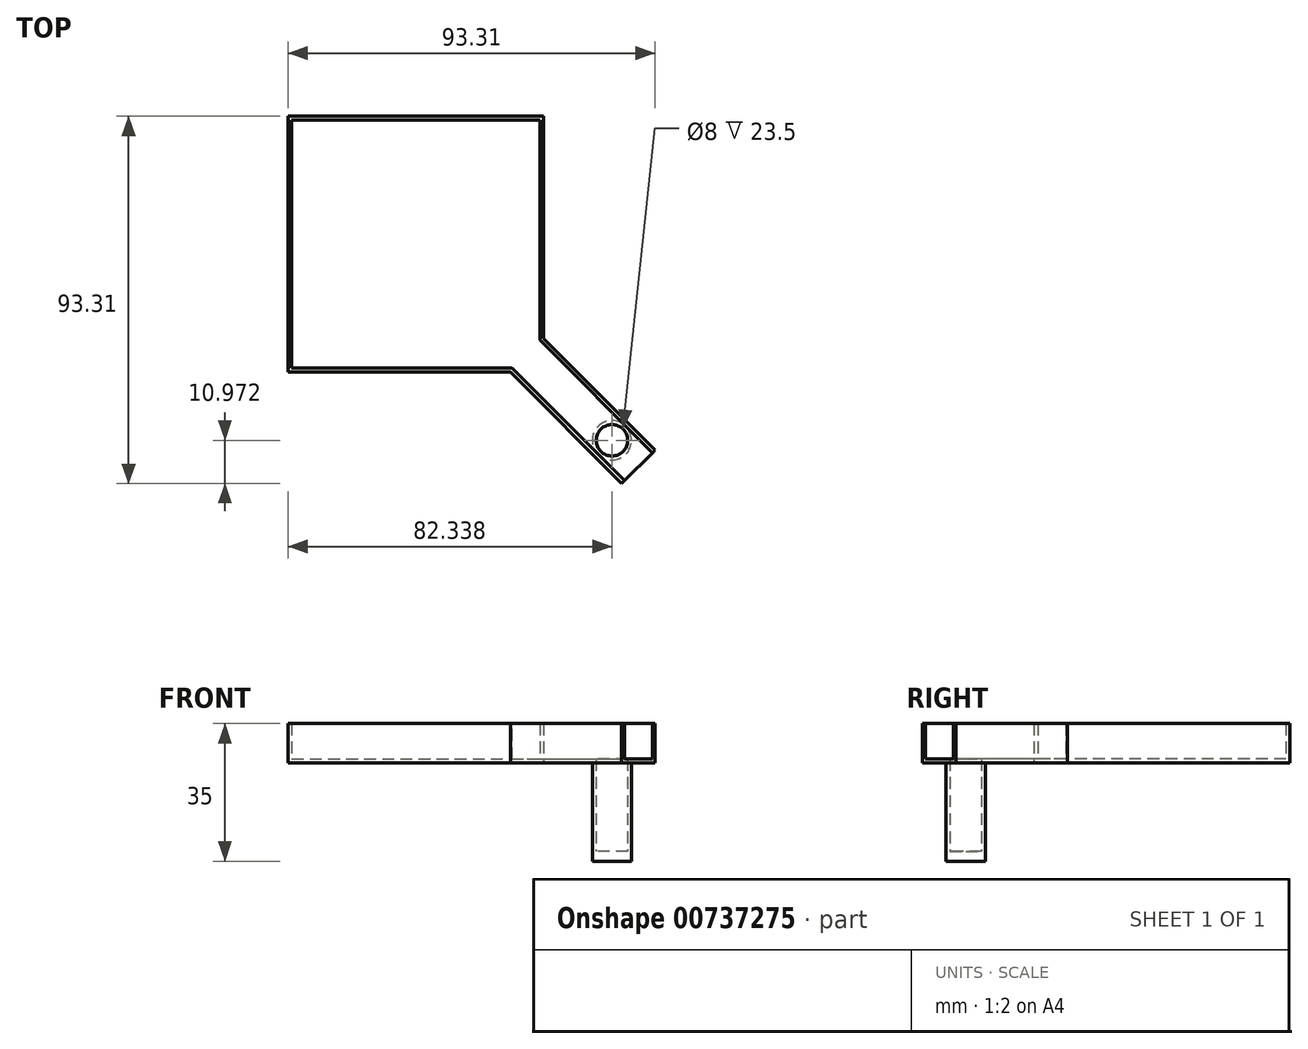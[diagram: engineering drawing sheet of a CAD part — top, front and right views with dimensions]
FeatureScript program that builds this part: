
annotation { "Feature Type Name" : "Feature", "Feature Type Description" : "" }
export const myFeature = defineFeature(function(context is Context, id is Id, definition is map)
    precondition{}
    {
        {
            var Q0;
            Q0=qCreatedBy(makeId("Top.planeOp"),FACE);
            var sketch = newSketch(context, id + "F0", { "sketchPlane" : qUnion([Q0])});
            skLineSegment(sketch, "E0", {"start": v(0, 44.12) * mm, "end": v(0, -39.93) * mm, "construction": true});
            skLineSegment(sketch, "E1", {"start": v(-43.3, 0) * mm, "end": v(40.23, 0) * mm, "construction": true});
            skLineSegment(sketch, "E2.bottom", {"start": v(-32.5, 32.5) * mm, "end": v(32.5, 32.5) * mm});
            skLineSegment(sketch, "E2.top", {"start": v(-32.5, -32.5) * mm, "end": v(32.5, -32.5) * mm});
            skLineSegment(sketch, "E2.left", {"start": v(-32.5, 32.5) * mm, "end": v(-32.5, -32.5) * mm});
            skLineSegment(sketch, "E2.right", {"start": v(32.5, 32.5) * mm, "end": v(32.5, -32.5) * mm});
            skSolve(sketch);
        }
        {
            var Q0;
            Q0 = qSketchRegion(id + "F0", true);
            extrude(context, id + "F1", {"entities" : qUnion([Q0]), "depth" : 10 * mm, "offsetDistance" : 25 * mm});
        }
        {
            var Q0;
            Q0=makeQuery(id+"F1.opExtrude","CAP_FACE",FACE,{"disambiguationData":[OSD([sQuery(id+"F0.wireOp",EDGE,"E2.bottom"),sQuery(id+"F0.wireOp",EDGE,"E2.top"),sQuery(id+"F0.wireOp",EDGE,"E2.left"),sQuery(id+"F0.wireOp",EDGE,"E2.right")])],"isStart":false});
            shell(context, id + "F2", {"entities" : qUnion([Q0]), "thickness" : 1 * mm});
        }
        {
            var Q0;
            Q0=qCreatedBy(makeId("Right.planeOp"),FACE);
            var Q1;
            Q1=qCreatedBy(makeId("Front.planeOp"),FACE);
            cPlane(context, id + "F3", {"entities" : qUnion([Q0, Q1]), "cplaneType" : CPlaneType.MID_PLANE, "offset" : 25 * mm, "flipAlignment" : true, "width" : 150 * mm, "height" : 150 * mm});
        }
        {
            var Q0;
            Q0=qCreatedBy(id+"F3.planeOp",FACE);
            cPlane(context, id + "F4", {"entities" : qUnion([Q0]), "cplaneType" : CPlaneType.OFFSET, "offset" : 50 * mm, "width" : 150 * mm, "height" : 150 * mm});
        }
        {
            var Q0;
            Q0=qCreatedBy(id+"F4.planeOp",FACE);
            var sketch = newSketch(context, id + "F5", { "sketchPlane" : qUnion([Q0])});
            skPoint(sketch, "E3.0", {"position": v(0, 5) * mm});
            skLineSegment(sketch, "E4.left", {"start": v(5, 10) * mm, "end": v(5, 1) * mm});
            skLineSegment(sketch, "E4.right", {"start": v(-5, 10) * mm, "end": v(-5, 1) * mm});
            skLineSegment(sketch, "E5.1", {"start": v(6, 0) * mm, "end": v(-6, 0) * mm});
            skLineSegment(sketch, "E5.2", {"start": v(-6, 10) * mm, "end": v(-6, 0) * mm});
            skLineSegment(sketch, "E6.0", {"start": v(5, 1) * mm, "end": v(-5, 1) * mm});
            skLineSegment(sketch, "E7", {"start": v(6, 0) * mm, "end": v(6, 10) * mm});
            skLineSegment(sketch, "E8", {"start": v(6, 10) * mm, "end": v(5, 10) * mm});
            skLineSegment(sketch, "E9", {"start": v(-5, 10) * mm, "end": v(-6, 10) * mm});
            skSolve(sketch);
        }
        {
            var Q0;
            Q0=makeQuery(id+"F5.imprint","IMPRINT",FACE,{"disambiguationData":[TD([[makeQuery(id+"F5.imprint","IMPRINT",EDGE,{"derivedFrom":sQuery(id+"F5.wireOp",EDGE,"E4.left")}),1.0]])]});
            var Q1;
            Q1=makeQuery(id+"F1.opExtrude","SWEPT_BODY",BODY,{"disambiguationData":[OSD([sQuery(id+"F0.wireOp",EDGE,"E2.bottom"),sQuery(id+"F0.wireOp",EDGE,"E2.top"),sQuery(id+"F0.wireOp",EDGE,"E2.left"),sQuery(id+"F0.wireOp",EDGE,"E2.right")])]});
            extrude(context, id + "F6", {"entities" : qUnion([Q0]), "operationType" : NewBodyOperationType.ADD, "endBound" : BoundingType.UP_TO_NEXT, "oppositeDirection" : true, "depth" : 25 * mm, "endBoundEntityBody" : qUnion([Q1]), "offsetDistance" : 25 * mm, "hasSecondDirection" : true, "secondDirectionOppositeDirection" : false, "secondDirectionDepth" : 30 * mm});
        }
        {
            var Q0;
            Q0=qCreatedBy(id+"F4.planeOp",FACE);
            var sketch = newSketch(context, id + "F7", { "sketchPlane" : qUnion([Q0])});
            skLineSegment(sketch, "E10.0", {"start": v(-5, 10) * mm, "end": v(-5, 1) * mm});
            skLineSegment(sketch, "E11.0", {"start": v(5, 1) * mm, "end": v(-5, 1) * mm});
            skLineSegment(sketch, "E12.0", {"start": v(5, 10) * mm, "end": v(5, 1) * mm});
            skLineSegment(sketch, "E13.0", {"start": v(5, 10) * mm, "end": v(0, 10) * mm});
            skLineSegment(sketch, "E14.0", {"start": v(-5, 10) * mm, "end": v(0, 10) * mm});
            skSolve(sketch);
        }
        {
            var Q0;
            Q0=makeQuery(id+"F7.imprint","IMPRINT",FACE,{"disambiguationData":[TD([[makeQuery(id+"F7.imprint","IMPRINT",EDGE,{"derivedFrom":sQuery(id+"F7.wireOp",EDGE,"E10.0")}),1.0]])]});
            extrude(context, id + "F8", {"entities" : qUnion([Q0]), "operationType" : NewBodyOperationType.REMOVE, "oppositeDirection" : true, "depth" : 64.9 * mm, "offsetDistance" : 25 * mm, "hasSecondDirection" : true, "secondDirectionBound" : SecondDirectionBoundingType.THROUGH_ALL, "secondDirectionOppositeDirection" : false, "secondDirectionDepth" : 25 * mm});
        }
        {
            var Q0;
            Q0=qCreatedBy(makeId("Top.planeOp"),FACE);
            var sketch = newSketch(context, id + "F9", { "sketchPlane" : qUnion([Q0])});
            skPoint(sketch, "E15.0", {"position": v(0, 0) * mm});
            skLineSegment(sketch, "E16", {"start": v(0, 0) * mm, "end": v(70.71, -70.71) * mm, "construction": true});
            skLineSegment(sketch, "E17", {"start": v(53.37, -46.3) * mm, "end": v(46.3, -53.37) * mm, "construction": true});
            skCircle(sketch, "E18", {"center": v(49.84, -49.84) * mm, "radius": 5 * mm});
            skSolve(sketch);
        }
        {
            var Q0;
            Q0=makeQuery(id+"F9.imprint","IMPRINT",FACE,{"disambiguationData":[TD([[makeQuery(id+"F9.imprint","IMPRINT",EDGE,{"derivedFrom":sQuery(id+"F9.wireOp",EDGE,"E18")}),1.0]])]});
            extrude(context, id + "F10", {"entities" : qUnion([Q0]), "operationType" : NewBodyOperationType.ADD, "oppositeDirection" : true, "depth" : 25 * mm, "offsetDistance" : 25 * mm, "hasSecondDirection" : true, "secondDirectionBound" : SecondDirectionBoundingType.UP_TO_NEXT, "secondDirectionOppositeDirection" : false, "secondDirectionDepth" : 25 * mm});
        }
        {
            var Q0;
            Q0=qCreatedBy(makeId("Top.planeOp"),FACE);
            var sketch = newSketch(context, id + "F11", { "sketchPlane" : qUnion([Q0])});
            skCircle(sketch, "E19", {"center": v(49.84, -49.84) * mm, "radius": 4 * mm});
            skSolve(sketch);
        }
        {
            var Q0;
            Q0 = qSketchRegion(id + "F11", true);
            var Q1;
            Q1=makeQuery(id+"F8.boolean.opBoolean","COPY",FACE,{"derivedFrom":makeQuery(id+"F8.opExtrude","SWEPT_FACE",FACE,{"disambiguationData":[OSD([sQuery(id+"F7.wireOp",EDGE,"ebyGRnMg-mdpS-d85R-b6UQ-0lTUfEDr3TMw")])]})});
            var Q2;
            Q2=makeQuery(id+"F10.opExtrude","CAP_FACE",FACE,{"disambiguationData":[OSD([sQuery(id+"F9.wireOp",EDGE,"E18")])],"isStart":false});
            extrude(context, id + "F12", {"entities" : qUnion([Q0]), "operationType" : NewBodyOperationType.REMOVE, "endBound" : BoundingType.UP_TO_NEXT, "depth" : 25 * mm, "endBoundEntityFace" : qUnion([Q1]), "offsetDistance" : 25 * mm, "hasSecondDirection" : true, "secondDirectionOppositeDirection" : true, "secondDirectionDepth" : 22.5 * mm, "secondDirectionBoundEntityFace" : qUnion([Q2])});
        }
    });
